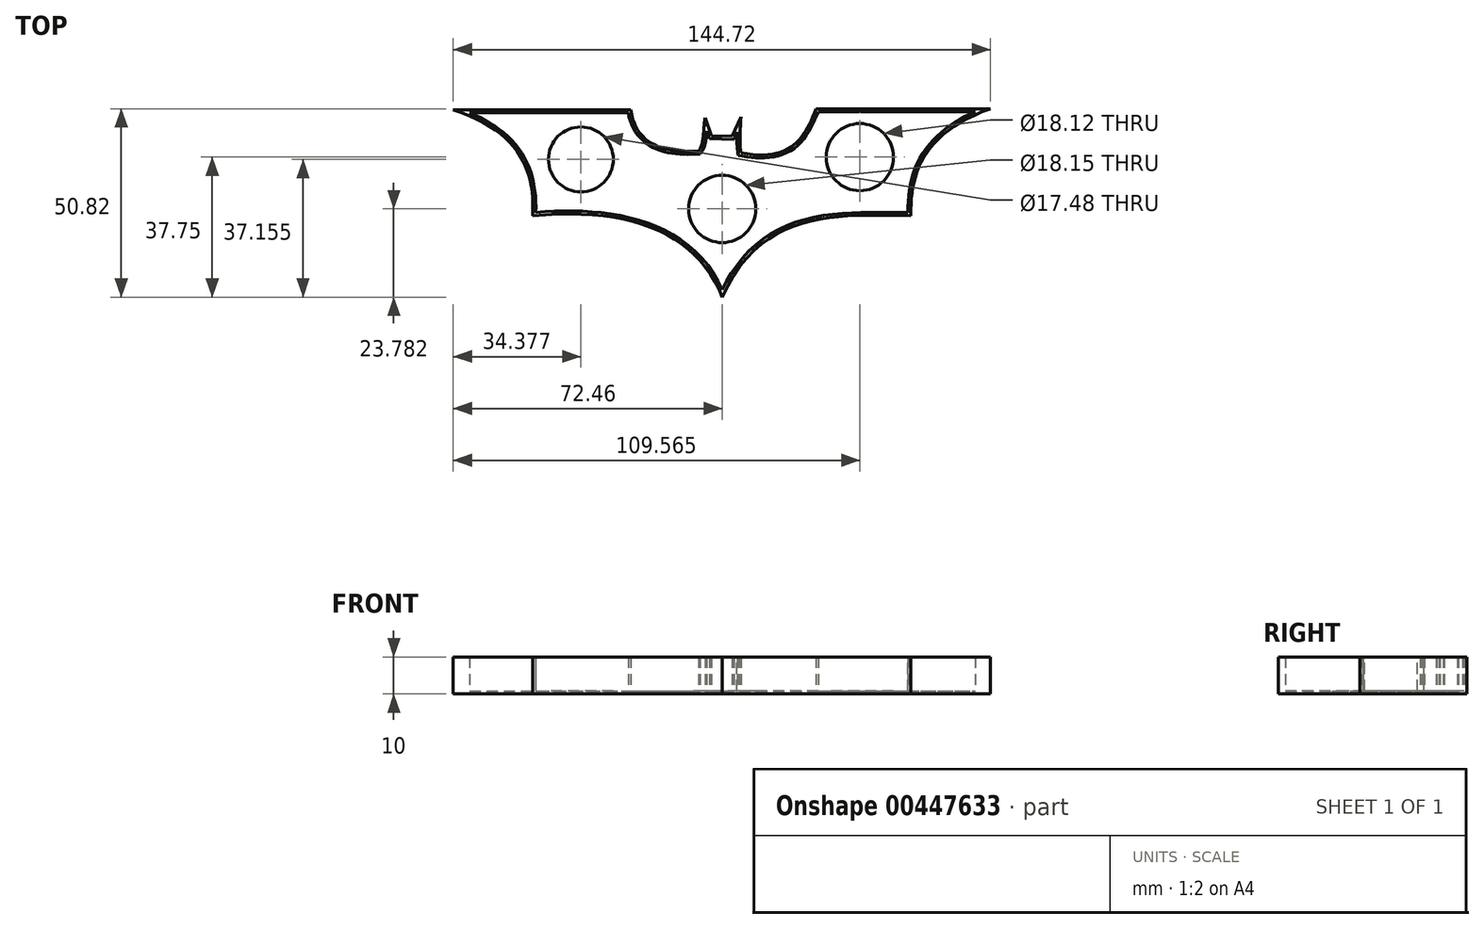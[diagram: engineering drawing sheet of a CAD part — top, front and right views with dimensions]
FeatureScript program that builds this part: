
annotation { "Feature Type Name" : "Feature", "Feature Type Description" : "" }
export const myFeature = defineFeature(function(context is Context, id is Id, definition is map)
    precondition{}
    {
        {
            var Q0;
            Q0=qCreatedBy(makeId("Top.planeOp"),FACE);
            var sketch = newSketch(context, id + "F0", { "sketchPlane" : qUnion([Q0])});
            skLineSegment(sketch, "E0", {"start": v(-72.46, 21.7) * mm, "end": v(-24.62, 21.7) * mm});
            skLineSegment(sketch, "E1", {"start": v(25.3, 22) * mm, "end": v(72.26, 22) * mm});
            skFitSpline(sketch, "E2", {"points": [v(-72.46, 21.7) * mm, v(-51.06, -6.83) * mm], "startDerivative": vector(53.5, -17.83) * mm, "endDerivative": vector(-1.78, -37.44) * mm});
            skFitSpline(sketch, "E3", {"points": [v(-51.06, -6.83) * mm, v(0, -28.83) * mm], "startDerivative": vector(80.24, 7.13) * mm, "endDerivative": vector(20.35, -51.7) * mm});
            skFitSpline(sketch, "E4", {"points": [v(0, -28.83) * mm, v(50.87, -6.83) * mm], "startDerivative": vector(32.24, 74) * mm, "endDerivative": vector(53.5, 0) * mm});
            skFitSpline(sketch, "E5", {"points": [v(50.87, -6.83) * mm, v(72.26, 22) * mm], "startDerivative": vector(-0.9, 35.66) * mm, "endDerivative": vector(53.5, 19.61) * mm});
            skFitSpline(sketch, "E6", {"points": [v(25.3, 22) * mm, v(5.02, 10.07) * mm], "startDerivative": vector(-9.8, -25.85) * mm, "endDerivative": vector(-39.23, 7.13) * mm});
            skFitSpline(sketch, "E7", {"points": [v(5.02, 10.07) * mm, v(5.02, 19.74) * mm], "startDerivative": vector(-0.98, 8.1) * mm, "endDerivative": vector(0.98, 20.92) * mm});
            skLineSegment(sketch, "E8", {"start": v(5.02, 19.74) * mm, "end": v(2.62, 14.54) * mm});
            skLineSegment(sketch, "E9", {"start": v(-2.9, 14.73) * mm, "end": v(2.62, 14.54) * mm});
            skLineSegment(sketch, "E10", {"start": v(-2.9, 14.73) * mm, "end": v(-4.62, 19.49) * mm});
            skFitSpline(sketch, "E11", {"points": [v(-4.62, 19.49) * mm, v(-6.39, 10.56) * mm], "startDerivative": vector(-1.77, -8.93) * mm, "endDerivative": vector(-5.07, -5.64) * mm});
            skFitSpline(sketch, "E12", {"points": [v(-24.62, 21.7) * mm, v(-6.39, 10.56) * mm], "startDerivative": vector(4.25, -31.33) * mm, "endDerivative": vector(22.38, 1.52) * mm});
            skSolve(sketch);
        }
        {
            var Q0;
            Q0=makeQuery(id+"F0.imprint","IMPRINT",FACE,{"disambiguationData":[TD([[makeQuery(id+"F0.imprint","IMPRINT",EDGE,{"derivedFrom":sQuery(id+"F0.wireOp",EDGE,"E0")}),-1.0]])]});
            extrude(context, id + "F1", {"entities" : qUnion([Q0]), "depth" : 10 * mm});
        }
        {
            var Q0;
            Q0=makeQuery(id+"F1.opExtrude","CAP_FACE",FACE,{"disambiguationData":[OSD([sQuery(id+"F0.wireOp",EDGE,"E0"),sQuery(id+"F0.wireOp",EDGE,"E1"),sQuery(id+"F0.wireOp",EDGE,"E2"),sQuery(id+"F0.wireOp",EDGE,"E3"),sQuery(id+"F0.wireOp",EDGE,"E4"),sQuery(id+"F0.wireOp",EDGE,"E5"),sQuery(id+"F0.wireOp",EDGE,"E6"),sQuery(id+"F0.wireOp",EDGE,"E7"),sQuery(id+"F0.wireOp",EDGE,"E8"),sQuery(id+"F0.wireOp",EDGE,"E9"),sQuery(id+"F0.wireOp",EDGE,"E10"),sQuery(id+"F0.wireOp",EDGE,"E11"),sQuery(id+"F0.wireOp",EDGE,"E12")])],"isStart":false});
            shell(context, id + "F2", {"entities" : qUnion([Q0]), "thickness" : 0.8 * mm});
        }
        {
            var Q0;
            Q0=makeQuery(id+"F2.opShell","OFFSET_FACE",FACE,{"disambiguationData":[OSD([sQuery(id+"F0.wireOp",EDGE,"E0"),sQuery(id+"F0.wireOp",EDGE,"E1"),sQuery(id+"F0.wireOp",EDGE,"E2"),sQuery(id+"F0.wireOp",EDGE,"E3"),sQuery(id+"F0.wireOp",EDGE,"E4"),sQuery(id+"F0.wireOp",EDGE,"E5"),sQuery(id+"F0.wireOp",EDGE,"E6"),sQuery(id+"F0.wireOp",EDGE,"E7"),sQuery(id+"F0.wireOp",EDGE,"E8"),sQuery(id+"F0.wireOp",EDGE,"E9"),sQuery(id+"F0.wireOp",EDGE,"E10"),sQuery(id+"F0.wireOp",EDGE,"E11"),sQuery(id+"F0.wireOp",EDGE,"E12")])]});
            var sketch = newSketch(context, id + "F3", { "sketchPlane" : qUnion([Q0])});
            skCircle(sketch, "E13", {"center": v(-38.08, 8.33) * mm, "radius": 8.74 * mm});
            skCircle(sketch, "E14", {"center": v(0, -5.05) * mm, "radius": 9.08 * mm});
            skCircle(sketch, "E15", {"center": v(37.1, 8.92) * mm, "radius": 9.06 * mm});
            skSolve(sketch);
        }
        {
            var Q0;
            Q0=makeQuery(id+"F3.imprint","IMPRINT",FACE,{"disambiguationData":[TD([[makeQuery(id+"F3.imprint","IMPRINT",EDGE,{"derivedFrom":sQuery(id+"F3.wireOp",EDGE,"E13")}),1.0]])]});
            var Q1;
            Q1=makeQuery(id+"F3.imprint","IMPRINT",FACE,{"disambiguationData":[TD([[makeQuery(id+"F3.imprint","IMPRINT",EDGE,{"derivedFrom":sQuery(id+"F3.wireOp",EDGE,"E14")}),1.0]])]});
            var Q2;
            Q2=makeQuery(id+"F3.imprint","IMPRINT",FACE,{"disambiguationData":[TD([[makeQuery(id+"F3.imprint","IMPRINT",EDGE,{"derivedFrom":sQuery(id+"F3.wireOp",EDGE,"E15")}),1.0]])]});
            extrude(context, id + "F4", {"entities" : qUnion([Q0, Q1, Q2]), "operationType" : NewBodyOperationType.REMOVE, "oppositeDirection" : true, "depth" : 25 * mm});
        }
    });
